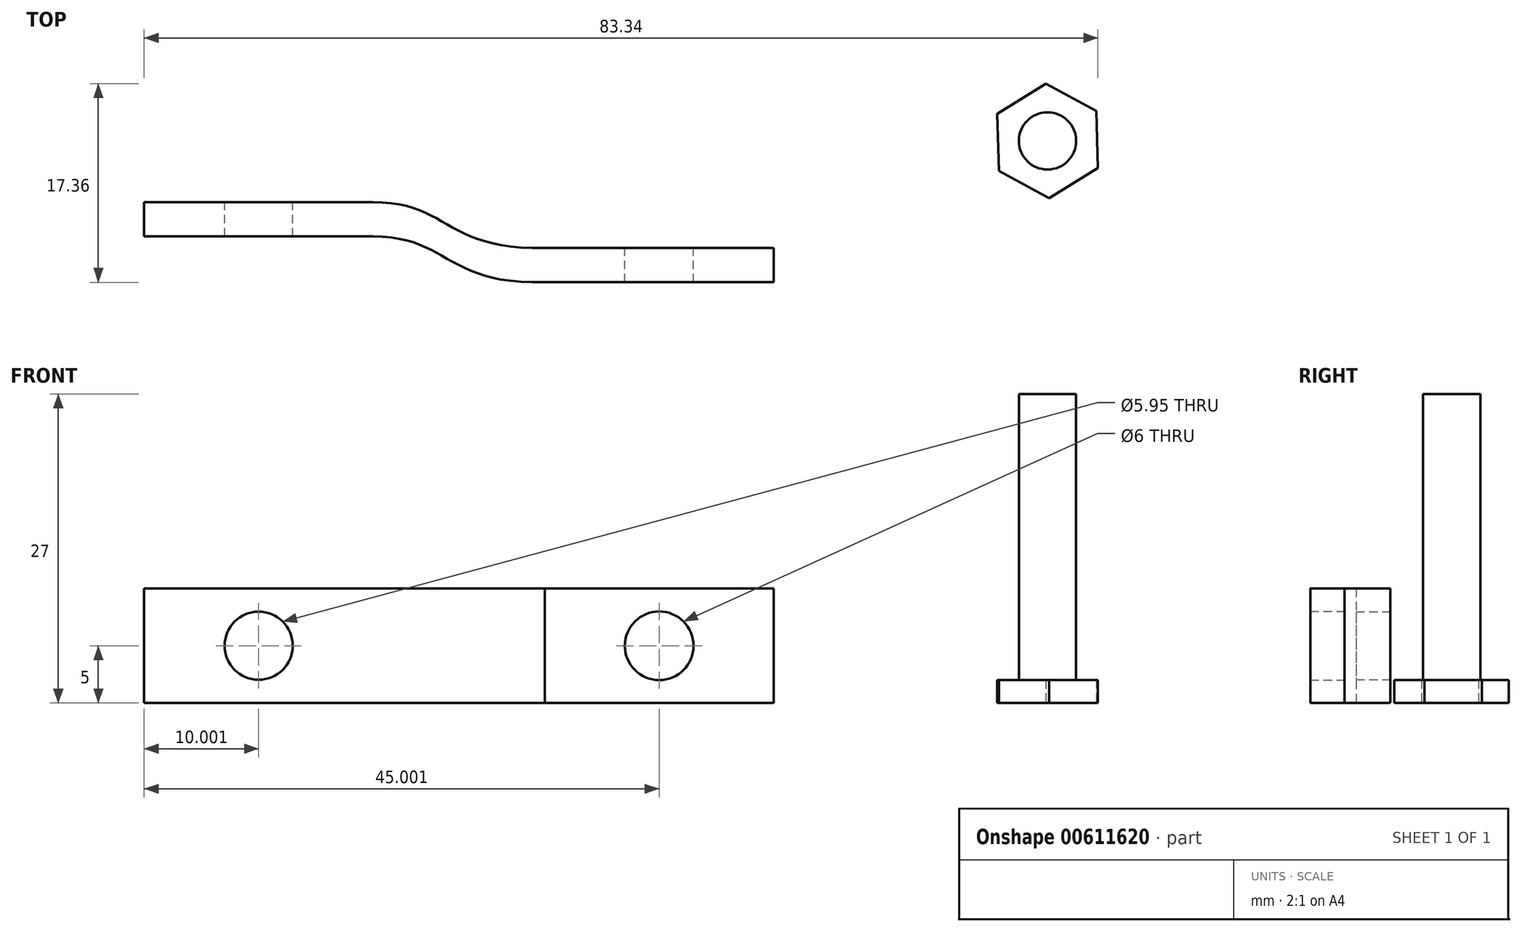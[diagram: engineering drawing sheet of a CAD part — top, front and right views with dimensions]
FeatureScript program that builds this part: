
annotation { "Feature Type Name" : "Feature", "Feature Type Description" : "" }
export const myFeature = defineFeature(function(context is Context, id is Id, definition is map)
    precondition{}
    {
        {
            var Q0;
            Q0=qCreatedBy(makeId("Top.planeOp"),FACE);
            var sketch = newSketch(context, id + "F0", { "sketchPlane" : qUnion([Q0])});
            skLineSegment(sketch, "E0", {"start": v(-49.78, 22.37) * mm, "end": v(-29.78, 22.37) * mm});
            skFitSpline(sketch, "E1", {"points": [v(-29.78, 22.37) * mm, v(-14.78, 18.37) * mm], "startDerivative": vector(19.93, 0) * mm, "endDerivative": vector(26.25, 0.62) * mm});
            skLineSegment(sketch, "E2", {"start": v(-14.78, 18.37) * mm, "end": v(5.22, 18.37) * mm});
            skLineSegment(sketch, "E3", {"start": v(-49.78, 22.37) * mm, "end": v(-49.78, 19.37) * mm});
            skLineSegment(sketch, "E4", {"start": v(-49.78, 19.37) * mm, "end": v(-29.78, 19.37) * mm});
            skFitSpline(sketch, "E5", {"points": [v(-29.78, 19.37) * mm, v(-14.78, 15.37) * mm], "startDerivative": vector(19.93, 0) * mm, "endDerivative": vector(26.25, 0.62) * mm});
            skLineSegment(sketch, "E6", {"start": v(-14.78, 15.37) * mm, "end": v(5.22, 15.37) * mm});
            skLineSegment(sketch, "E7", {"start": v(5.22, 18.37) * mm, "end": v(5.22, 15.37) * mm});
            skSolve(sketch);
        }
        {
            var Q0;
            Q0=makeQuery(id+"F0.imprint","IMPRINT",FACE,{"disambiguationData":[TD([[makeQuery(id+"F0.imprint","IMPRINT",EDGE,{"derivedFrom":sQuery(id+"F0.wireOp",EDGE,"E0")}),-1.0]])]});
            extrude(context, id + "F1", {"entities" : qUnion([Q0]), "depth" : 10 * mm, "offsetDistance" : 25 * mm});
        }
        {
            var Q0;
            Q0=makeQuery(id+"F1.opExtrude","SWEPT_FACE",FACE,{"disambiguationData":[OSD([sQuery(id+"F0.wireOp",EDGE,"E0")])]});
            var sketch = newSketch(context, id + "F2", { "sketchPlane" : qUnion([Q0])});
            skCircle(sketch, "E8", {"center": v(39.78, 5) * mm, "radius": 2.97 * mm});
            skSolve(sketch);
        }
        {
            var Q0;
            Q0=makeQuery(id+"F2.imprint","IMPRINT",FACE,{"disambiguationData":[TD([[makeQuery(id+"F2.imprint","IMPRINT",EDGE,{"derivedFrom":sQuery(id+"F2.wireOp",EDGE,"E8")}),1.0]])]});
            extrude(context, id + "F3", {"entities" : qUnion([Q0]), "operationType" : NewBodyOperationType.REMOVE, "endBound" : BoundingType.UP_TO_NEXT, "oppositeDirection" : true, "depth" : 3 * mm, "offsetDistance" : 25 * mm});
        }
        {
            var Q0;
            Q0=makeQuery(id+"F1.opExtrude","SWEPT_FACE",FACE,{"disambiguationData":[OSD([sQuery(id+"F0.wireOp",EDGE,"E2")])]});
            var sketch = newSketch(context, id + "F4", { "sketchPlane" : qUnion([Q0])});
            skCircle(sketch, "E9", {"center": v(4.78, 5) * mm, "radius": 3 * mm});
            skSolve(sketch);
        }
        {
            var Q0;
            Q0=makeQuery(id+"F4.imprint","IMPRINT",FACE,{"disambiguationData":[TD([[makeQuery(id+"F4.imprint","IMPRINT",EDGE,{"derivedFrom":sQuery(id+"F4.wireOp",EDGE,"E9")}),1.0]])]});
            extrude(context, id + "F5", {"entities" : qUnion([Q0]), "operationType" : NewBodyOperationType.REMOVE, "endBound" : BoundingType.UP_TO_NEXT, "oppositeDirection" : true, "depth" : 25 * mm, "offsetDistance" : 25 * mm});
        }
        {
            var Q0;
            Q0=qCreatedBy(makeId("Top.planeOp"),FACE);
            var sketch = newSketch(context, id + "F6", { "sketchPlane" : qUnion([Q0])});
            skCircle(sketch, "E10.cCircle", {"center": v(29.16, 27.72) * mm, "radius": 5 * mm, "construction": true});
            skLineSegment(sketch, "E10.0", {"start": v(24.75, 30.1) * mm, "end": v(29, 32.72) * mm});
            skLineSegment(sketch, "E10.1", {"start": v(29, 32.72) * mm, "end": v(33.4, 30.35) * mm});
            skLineSegment(sketch, "E10.2", {"start": v(33.4, 30.35) * mm, "end": v(33.56, 25.35) * mm});
            skLineSegment(sketch, "E10.3", {"start": v(33.56, 25.35) * mm, "end": v(29.3, 22.72) * mm});
            skLineSegment(sketch, "E10.4", {"start": v(29.3, 22.72) * mm, "end": v(24.9, 25.1) * mm});
            skLineSegment(sketch, "E10.5", {"start": v(24.9, 25.1) * mm, "end": v(24.75, 30.1) * mm});
            skSolve(sketch);
        }
        {
            var Q0;
            Q0=makeQuery(id+"F6.imprint","IMPRINT",FACE,{"disambiguationData":[TD([[makeQuery(id+"F6.imprint","IMPRINT",EDGE,{"derivedFrom":sQuery(id+"F6.wireOp",EDGE,"E10.0")}),-1.0]])]});
            extrude(context, id + "F7", {"entities" : qUnion([Q0]), "depth" : 2 * mm, "offsetDistance" : 25 * mm});
        }
        {
            var Q0;
            Q0=makeQuery(id+"F7.opExtrude","CAP_FACE",FACE,{"disambiguationData":[OSD([sQuery(id+"F6.wireOp",EDGE,"E10.0"),sQuery(id+"F6.wireOp",EDGE,"E10.1"),sQuery(id+"F6.wireOp",EDGE,"E10.2"),sQuery(id+"F6.wireOp",EDGE,"E10.3"),sQuery(id+"F6.wireOp",EDGE,"E10.4"),sQuery(id+"F6.wireOp",EDGE,"E10.5")])],"isStart":false});
            var sketch = newSketch(context, id + "F8", { "sketchPlane" : qUnion([Q0])});
            skLineSegment(sketch, "E11", {"start": v(29, 32.72) * mm, "end": v(29.3, 22.72) * mm, "construction": true});
            skLineSegment(sketch, "E12", {"start": v(24.75, 30.1) * mm, "end": v(33.56, 25.35) * mm, "construction": true});
            skCircle(sketch, "E13", {"center": v(29.16, 27.72) * mm, "radius": 2.5 * mm});
            skSolve(sketch);
        }
        {
            var Q0;
            Q0=makeQuery(id+"F8.imprint","IMPRINT",FACE,{"disambiguationData":[TD([[makeQuery(id+"F8.imprint","IMPRINT",EDGE,{"derivedFrom":sQuery(id+"F8.wireOp",EDGE,"E13")}),1.0]])]});
            extrude(context, id + "F9", {"entities" : qUnion([Q0]), "operationType" : NewBodyOperationType.ADD, "depth" : 25 * mm, "offsetDistance" : 25 * mm});
        }
    });
